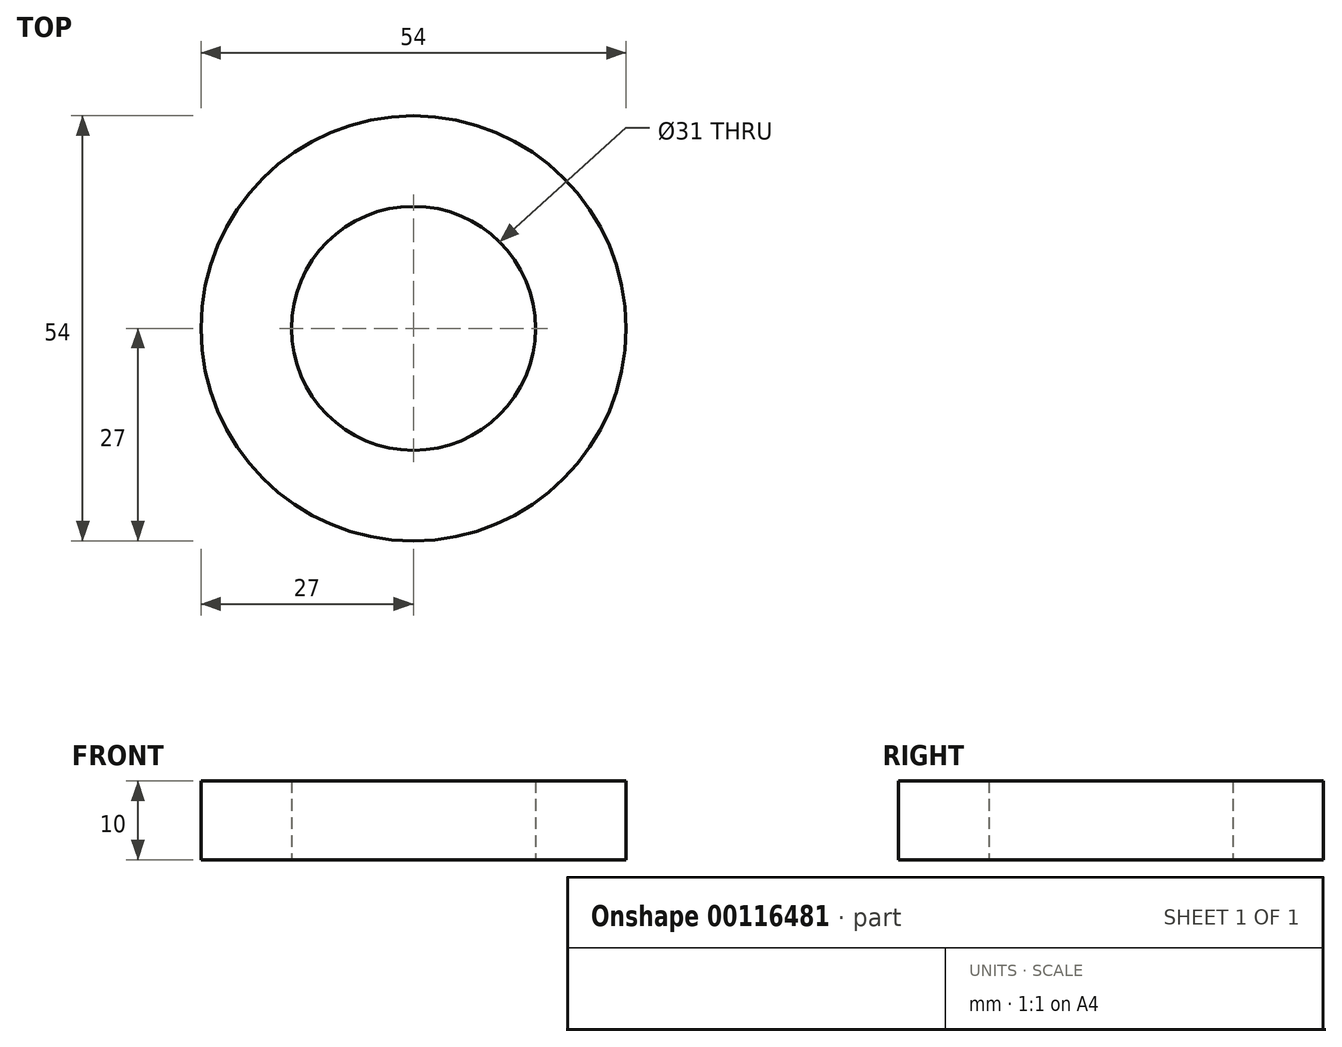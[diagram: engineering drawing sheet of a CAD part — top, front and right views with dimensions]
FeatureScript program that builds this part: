
annotation { "Feature Type Name" : "Feature", "Feature Type Description" : "" }
export const myFeature = defineFeature(function(context is Context, id is Id, definition is map)
    precondition{}
    {
        {
            var Q0;
            Q0=qCreatedBy(makeId("Top.planeOp"),FACE);
            var sketch = newSketch(context, id + "F0", { "sketchPlane" : qUnion([Q0])});
            skCircle(sketch, "E0", {"center": v(0, 0) * mm, "radius": 15.5 * mm});
            skCircle(sketch, "E1", {"center": v(0, 0) * mm, "radius": 27 * mm});
            skSolve(sketch);
        }
        {
            var Q0;
            Q0=makeQuery(id+"F0.imprint","IMPRINT",FACE,{"disambiguationData":[TD([[makeQuery(id+"F0.imprint","IMPRINT",EDGE,{"derivedFrom":sQuery(id+"F0.wireOp",EDGE,"E0")}),-1.0]])]});
            extrude(context, id + "F1", {"entities" : qUnion([Q0]), "depth" : 10 * mm});
        }
    });
